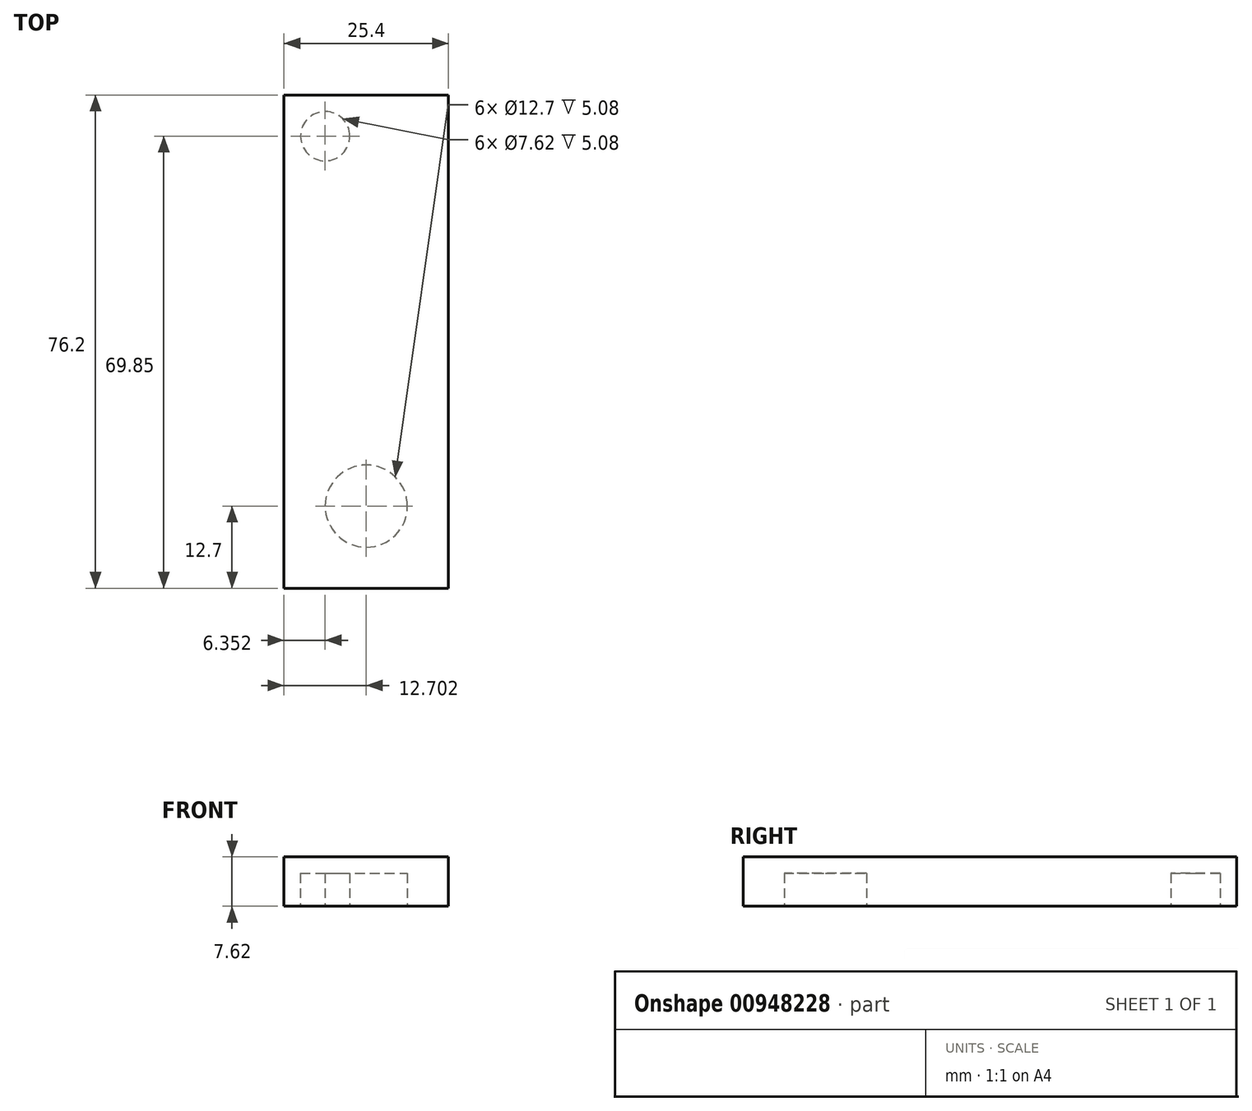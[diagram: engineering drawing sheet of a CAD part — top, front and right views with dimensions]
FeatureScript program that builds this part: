
annotation { "Feature Type Name" : "Feature", "Feature Type Description" : "" }
export const myFeature = defineFeature(function(context is Context, id is Id, definition is map)
    precondition{}
    {
        {
            var Q0;
            Q0=qCreatedBy(makeId("Top.planeOp"),FACE);
            var sketch = newSketch(context, id + "F0", { "sketchPlane" : qUnion([Q0])});
            skLineSegment(sketch, "E0.bottom", {"start": v(-16, 48.99) * mm, "end": v(9.4, 48.99) * mm});
            skLineSegment(sketch, "E0.top", {"start": v(-16, -27.21) * mm, "end": v(9.4, -27.21) * mm});
            skLineSegment(sketch, "E0.left", {"start": v(-16, 48.99) * mm, "end": v(-16, -27.21) * mm});
            skLineSegment(sketch, "E0.right", {"start": v(9.4, 48.99) * mm, "end": v(9.4, -27.21) * mm});
            skSolve(sketch);
        }
        {
            var Q0;
            Q0=makeQuery(id+"F0.imprint","IMPRINT",FACE,{"disambiguationData":[TD([[makeQuery(id+"F0.imprint","IMPRINT",EDGE,{"derivedFrom":sQuery(id+"F0.wireOp",EDGE,"E0.bottom")}),-1.0]])]});
            extrude(context, id + "F1", {"entities" : qUnion([Q0]), "depth" : 7.62 * mm, "offsetDistance" : 25.4 * mm});
        }
        {
            var Q0;
            Q0=makeQuery(id+"F1.opExtrude","CAP_FACE",FACE,{"disambiguationData":[OSD([sQuery(id+"F0.wireOp",EDGE,"E0.bottom"),sQuery(id+"F0.wireOp",EDGE,"E0.top"),sQuery(id+"F0.wireOp",EDGE,"E0.left"),sQuery(id+"F0.wireOp",EDGE,"E0.right")])],"isStart":true});
            var sketch = newSketch(context, id + "F2", { "sketchPlane" : qUnion([Q0])});
            skCircle(sketch, "E1", {"center": v(-3.3, 14.51) * mm, "radius": 6.35 * mm});
            skPoint(sketch, "E1.centerSnap0", {"position": v(-3.3, 27.21) * mm});
            skSolve(sketch);
        }
        {
            var Q0;
            Q0=makeQuery(id+"F2.imprint","IMPRINT",FACE,{"disambiguationData":[TD([[makeQuery(id+"F2.imprint","IMPRINT",EDGE,{"derivedFrom":sQuery(id+"F2.wireOp",EDGE,"E1")}),1.0]])]});
            extrude(context, id + "F3", {"entities" : qUnion([Q0]), "operationType" : NewBodyOperationType.REMOVE, "oppositeDirection" : true, "depth" : 5.08 * mm, "offsetDistance" : 25.4 * mm});
        }
        {
            var Q0;
            Q0=makeQuery(id+"F1.opExtrude","CAP_FACE",FACE,{"disambiguationData":[OSD([sQuery(id+"F0.wireOp",EDGE,"E0.bottom"),sQuery(id+"F0.wireOp",EDGE,"E0.top"),sQuery(id+"F0.wireOp",EDGE,"E0.left"),sQuery(id+"F0.wireOp",EDGE,"E0.right")])],"isStart":true});
            var sketch = newSketch(context, id + "F4", { "sketchPlane" : qUnion([Q0])});
            skCircle(sketch, "E2", {"center": v(-9.66, -42.64) * mm, "radius": 3.81 * mm});
            skSolve(sketch);
        }
        {
            var Q0;
            Q0=makeQuery(id+"F4.imprint","IMPRINT",FACE,{"disambiguationData":[TD([[makeQuery(id+"F4.imprint","IMPRINT",EDGE,{"derivedFrom":sQuery(id+"F4.wireOp",EDGE,"E2")}),1.0]])]});
            extrude(context, id + "F5", {"entities" : qUnion([Q0]), "operationType" : NewBodyOperationType.REMOVE, "oppositeDirection" : true, "depth" : 5.08 * mm, "offsetDistance" : 25.4 * mm});
        }
    });
